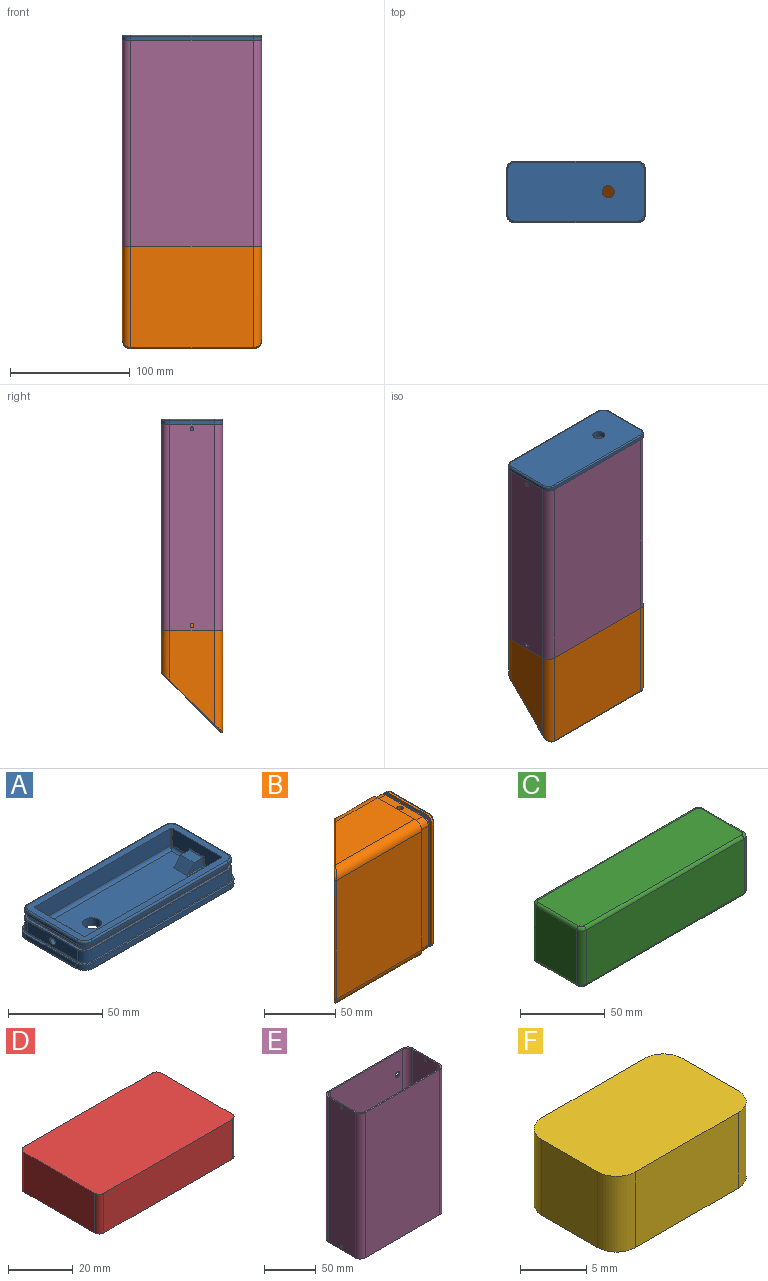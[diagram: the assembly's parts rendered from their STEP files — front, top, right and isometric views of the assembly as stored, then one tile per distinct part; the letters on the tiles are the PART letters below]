
ASSEMBLY  parts=6 mates=8
PART A: 138 faces, bbox 117.3x52.3x18.2 mm
  f0: cylinder r=0.5mm len=4mm, axis (0,0,-1), area 3.1mm2, adj f1,f3,f10,f116
  f1: torus R=1.5mm, axis (0,-1,0), area 2.2mm2, adj f0,f2,f3,f112
  f2: cylinder r=0.5mm len=10.03mm, axis (1,0,0), area 7.7mm2, adj f1,f3,f11,f12
  f3: plane 11.12x5.5mm, normal (0,1,0), area 48mm2, adj f0,f1,f2,f10,f11
  f4: cylinder r=0.5mm len=10.03mm, axis (-1,0,0), area 7.7mm2, adj f5,f7,f11,f12
  f5: torus R=1.5mm, axis (0,1,0), area 2.2mm2, adj f4,f6,f7,f13
  f6: cylinder r=0.5mm len=4mm, axis (0,0,1), area 3.1mm2, adj f5,f7,f10,f116
  f7: plane 11.12x5.5mm, normal (0,-1,0), area 48mm2, adj f4,f5,f6,f10,f11
  f8: cylinder r=2mm len=10mm, axis (1,0,0), area 125.7mm2, adj f9,f133
  f9: plane 4x4mm, normal (-1,0,0), area 12.6mm2, adj f8
  f10: plane 11x7mm, normal (0,0,1), area 70.1mm2, adj f0,f3,f6,f7,f11,f116
  f11: plane 11.18x6.18mm, normal (0.77,0,0.64), area 78.5mm2, adj f2,f3,f4,f7,f10,f12
  f12: plane 99x34mm, normal (0,0,1), area 3066.7mm2, adj f2,f4,f11,f13,f16,f20,f26,f28
  f13: cylinder r=2mm len=13mm, axis (0,-1,0), area 38.5mm2, adj f5,f12,f105,f116
  f14: cylinder r=0.5mm len=4.5mm, axis (0,0,-1), area 3.3mm2, adj f15,f19,f21,f27
  f15: cylinder r=0.5mm len=11mm, axis (0,-1,0), area 8.2mm2, adj f14,f18,f22,f27
  f16: cylinder r=0.5mm len=10.03mm, axis (1,0,0), area 7.7mm2, adj f12,f17,f23,f26
  f17: torus R=1.5mm, axis (0,-1,0), area 2.2mm2, adj f16,f18,f23,f110
  f18: cylinder r=0.5mm len=4.5mm, axis (0,0,1), area 3.3mm2, adj f15,f17,f23,f27
  f19: torus R=1.5mm, axis (0,1,0), area 2.2mm2, adj f14,f20,f21,f28
  f20: cylinder r=0.5mm len=10.03mm, axis (-1,0,0), area 7.7mm2, adj f12,f19,f21,f26
  f21: plane 11.12x5.5mm, normal (0,-1,0), area 48mm2, adj f14,f19,f20,f22,f26
  f22: plane 10x6.5mm, normal (0,0,1), area 65mm2, adj f15,f21,f23,f26
  f23: plane 11.12x5.5mm, normal (0,1,0), area 48mm2, adj f16,f17,f18,f22,f26
  f24: cylinder r=2mm len=10mm, axis (1,0,0), area 125.7mm2, adj f25,f37
  f25: plane 4x4mm, normal (1,0,0), area 12.6mm2, adj f24
  f26: plane 11.18x6.18mm, normal (-0.77,0,0.64), area 78.5mm2, adj f12,f16,f20,f21,f22,f23
  f27: plane 37x11mm, normal (-1,0,0), area 357.5mm2, adj f14,f15,f18,f28,f54,f110,f114,f115
  f28: cylinder r=2mm len=13mm, axis (0,1,0), area 38.5mm2, adj f12,f19,f27,f108
  f29: torus R=6mm, axis (0,0,1), area 7mm2, adj f30,f36,f40,f41
  f30: cylinder r=0.5mm len=37mm, axis (0,-1,0), area 29.1mm2, adj f29,f31,f41,f133
  f31: torus R=6mm, axis (0,0,1), area 7mm2, adj f30,f32,f41,f65
  f32: cylinder r=0.5mm len=102mm, axis (1,0,0), area 80.1mm2, adj f31,f33,f41,f64
  f33: torus R=6mm, axis (0,0,1), area 7mm2, adj f32,f34,f41,f63
  f34: cylinder r=0.5mm len=37mm, axis (0,1,0), area 29.1mm2, adj f33,f35,f37,f41
  f35: torus R=6mm, axis (0,0,1), area 7mm2, adj f34,f36,f38,f41
  f36: cylinder r=0.5mm len=102mm, axis (-1,0,0), area 80.1mm2, adj f29,f35,f39,f41
  f37: plane 37x7.3mm, normal (1,0,0), area 257.5mm2, adj f24,f34,f38,f60,f63
  f38: cylinder r=5.5mm len=7.3mm, axis (0,0,-1), area 63.1mm2, adj f35,f37,f39,f59
  f39: plane 102x7.3mm, normal (0,1,0), area 744.6mm2, adj f36,f38,f40,f58
  f40: cylinder r=5.5mm len=7.3mm, axis (0,0,-1), area 63.1mm2, adj f29,f39,f57,f133
  f41: plane 116x51mm, normal (0,0,1), area 318.8mm2, adj f29,f30,f31,f32,f33,f34,f35,f36
  f42: torus R=4.5mm, axis (0,0,1), area 12.7mm2, adj f43,f49,f53,f54
  f43: cylinder r=1mm len=37mm, axis (0,1,0), area 58.1mm2, adj f42,f44,f52,f54
  f44: torus R=4.5mm, axis (0,0,1), area 12.7mm2, adj f43,f45,f51,f54
  f45: cylinder r=1mm len=102mm, axis (-1,0,0), area 160.2mm2, adj f44,f46,f50,f54
  f46: torus R=4.5mm, axis (0,0,1), area 12.7mm2, adj f45,f47,f54,f103
  f47: cylinder r=1mm len=37mm, axis (0,-1,0), area 58.1mm2, adj f46,f48,f54,f75
  f48: torus R=4.5mm, axis (0,0,1), area 12.7mm2, adj f47,f49,f54,f76
  f49: cylinder r=1mm len=102mm, axis (1,0,0), area 160.2mm2, adj f42,f48,f54,f77
  f50: plane 102x1.8mm, normal (0,1,0), area 183.6mm2, adj f45,f51,f70,f103
  f51: cylinder r=5.5mm len=5.5mm, axis (0,0,-1), area 15.6mm2, adj f44,f50,f52,f69
  f52: plane 37x1.8mm, normal (1,0,0), area 66.6mm2, adj f43,f51,f53,f68
  f53: cylinder r=5.5mm len=5.5mm, axis (0,0,-1), area 15.6mm2, adj f42,f52,f67,f77
  f54: plane 111x46mm, normal (0,0,1), area 1174.8mm2, adj f27,f42,f43,f44,f45,f46,f47,f48
  f55: torus R=5.3mm, axis (0,0,-1), area 2.7mm2, adj f56,f62,f65,f66
  f56: cylinder r=0.2mm len=37mm, axis (0,1,0), area 11.6mm2, adj f55,f57,f66,f133
  f57: torus R=5.3mm, axis (0,0,-1), area 2.7mm2, adj f40,f56,f58,f66
  f58: cylinder r=0.2mm len=102mm, axis (1,0,0), area 32mm2, adj f39,f57,f59,f66
  f59: torus R=5.3mm, axis (0,0,-1), area 2.7mm2, adj f38,f58,f60,f66
  f60: cylinder r=0.2mm len=37mm, axis (0,-1,0), area 11.6mm2, adj f37,f59,f61,f66
  f61: torus R=5.3mm, axis (0,0,-1), area 2.7mm2, adj f60,f62,f63,f66
  f62: cylinder r=0.2mm len=102mm, axis (-1,0,0), area 32mm2, adj f55,f61,f64,f66
  f63: cylinder r=5.5mm len=7.3mm, axis (0,0,-1), area 63.1mm2, adj f33,f37,f61,f64
  f64: plane 102x7.3mm, normal (0,-1,0), area 744.6mm2, adj f32,f62,f63,f65
  f65: cylinder r=5.5mm len=7.3mm, axis (0,0,-1), area 63.1mm2, adj f31,f55,f64,f133
  f66: plane 112.6x47.6mm, normal (0,0,1), area 459.9mm2, adj f55,f56,f57,f58,f59,f60,f61,f62
  f67: torus R=5.3mm, axis (0,0,1), area 2.7mm2, adj f53,f68,f74,f78
  f68: cylinder r=0.2mm len=37mm, axis (0,1,0), area 11.6mm2, adj f52,f67,f69,f78
  f69: torus R=5.3mm, axis (0,0,1), area 2.7mm2, adj f51,f68,f70,f78
  f70: cylinder r=0.2mm len=102mm, axis (-1,0,0), area 32mm2, adj f50,f69,f71,f78
  f71: torus R=5.3mm, axis (0,0,1), area 2.7mm2, adj f70,f72,f78,f103
  f72: cylinder r=0.2mm len=37mm, axis (0,-1,0), area 11.6mm2, adj f71,f73,f75,f78
  f73: torus R=5.3mm, axis (0,0,1), area 2.7mm2, adj f72,f74,f76,f78
  f74: cylinder r=0.2mm len=102mm, axis (1,0,0), area 32mm2, adj f67,f73,f77,f78
  f75: plane 37x1.8mm, normal (-1,0,0), area 66.6mm2, adj f47,f72,f76,f103
  f76: cylinder r=5.5mm len=5.5mm, axis (0,0,-1), area 15.6mm2, adj f48,f73,f75,f77
  f77: plane 102x1.8mm, normal (0,-1,0), area 183.6mm2, adj f49,f53,f74,f76
  f78: plane 112.6x47.6mm, normal (0,0,-1), area 459.9mm2, adj f67,f68,f69,f70,f71,f72,f73,f74
  f79: torus R=3.8mm, axis (0,0,-1), area 2.7mm2, adj f66,f80,f86,f90
  f80: cylinder r=0.3mm len=37mm, axis (0,1,0), area 17.4mm2, adj f66,f79,f81,f89
  f81: torus R=3.8mm, axis (0,0,-1), area 2.7mm2, adj f66,f80,f82,f88
  f82: cylinder r=0.3mm len=102mm, axis (1,0,0), area 48.1mm2, adj f66,f81,f83,f87
  f83: torus R=3.8mm, axis (0,0,-1), area 2.7mm2, adj f66,f82,f84,f102
  f84: cylinder r=0.3mm len=37mm, axis (0,-1,0), area 17.4mm2, adj f66,f83,f85,f99
  f85: torus R=3.8mm, axis (0,0,-1), area 2.7mm2, adj f66,f84,f86,f100
  f86: cylinder r=0.3mm len=102mm, axis (-1,0,0), area 48.1mm2, adj f66,f79,f85,f101
  f87: plane 102x2.4mm, normal (0,1,0), area 244.8mm2, adj f82,f88,f94,f102
  f88: cylinder r=3.5mm len=3.5mm, axis (0,0,-1), area 13.2mm2, adj f81,f87,f89,f93
  f89: plane 37x2.4mm, normal (-1,0,0), area 88.8mm2, adj f80,f88,f90,f92
  f90: cylinder r=3.5mm len=3.5mm, axis (0,0,-1), area 13.2mm2, adj f79,f89,f91,f101
  f91: torus R=3.8mm, axis (0,0,-1), area 2.7mm2, adj f78,f90,f92,f98
  f92: cylinder r=0.3mm len=37mm, axis (0,1,0), area 17.4mm2, adj f78,f89,f91,f93
  f93: torus R=3.8mm, axis (0,0,-1), area 2.7mm2, adj f78,f88,f92,f94
  f94: cylinder r=0.3mm len=102mm, axis (1,0,0), area 48.1mm2, adj f78,f87,f93,f95
  f95: torus R=3.8mm, axis (0,0,-1), area 2.7mm2, adj f78,f94,f96,f102
  f96: cylinder r=0.3mm len=37mm, axis (0,-1,0), area 17.4mm2, adj f78,f95,f97,f99
  f97: torus R=3.8mm, axis (0,0,-1), area 2.7mm2, adj f78,f96,f98,f100
  f98: cylinder r=0.3mm len=102mm, axis (-1,0,0), area 48.1mm2, adj f78,f91,f97,f101
  f99: plane 37x2.4mm, normal (1,0,0), area 88.8mm2, adj f84,f96,f100,f102
  f100: cylinder r=3.5mm len=3.5mm, axis (0,0,-1), area 13.2mm2, adj f85,f97,f99,f101
  f101: plane 102x2.4mm, normal (0,-1,0), area 244.8mm2, adj f86,f90,f98,f100
  f102: cylinder r=3.5mm len=3.5mm, axis (0,0,-1), area 13.2mm2, adj f83,f87,f95,f99
  f103: cylinder r=5.5mm len=5.5mm, axis (0,0,-1), area 15.6mm2, adj f46,f50,f71,f75
  f104: cylinder r=5mm len=10mm, axis (0,0,-1), area 157.1mm2, adj f12,f132
  f105: bspline ~2x2mm, area 1.1mm2, adj f13,f109,f117
  f106: bspline ~2x2mm, area 1.1mm2, adj f111,f112,f119
  f107: bspline ~2x2mm, area 1.1mm2, adj f110,f111,f114
  f108: bspline ~2x2mm, area 1.1mm2, adj f28,f109,f115
  f109: cylinder r=2mm len=102mm, axis (1,0,0), area 315.7mm2, adj f12,f105,f108,f118
  f110: cylinder r=2mm len=13mm, axis (0,1,0), area 38.5mm2, adj f12,f17,f27,f107
  f111: cylinder r=2mm len=102mm, axis (-1,0,0), area 315.7mm2, adj f12,f106,f107,f113
  f112: cylinder r=2mm len=13mm, axis (0,-1,0), area 38.5mm2, adj f1,f12,f106,f116
  f113: plane 102x11mm, normal (0,-1,0), area 1122mm2, adj f54,f111,f114,f119
  f114: cylinder r=0.5mm len=11mm, axis (0,0,-1), area 8.6mm2, adj f27,f54,f107,f113
  f115: cylinder r=0.5mm len=11mm, axis (0,0,-1), area 8.6mm2, adj f27,f54,f108,f118
  f116: plane 37x11mm, normal (1,0,0), area 363mm2, adj f0,f6,f10,f13,f54,f112,f117,f119
  f117: cylinder r=0.5mm len=11mm, axis (0,0,-1), area 8.6mm2, adj f54,f105,f116,f118
  f118: plane 102x11mm, normal (0,1,0), area 1122mm2, adj f54,f109,f115,f117
  f119: cylinder r=0.5mm len=11mm, axis (0,0,-1), area 8.6mm2, adj f54,f106,f113,f116
  f120: torus R=6mm, axis (0,0,1), area 16.4mm2, adj f121,f127,f131,f132
  f121: cylinder r=1mm len=37mm, axis (0,-1,0), area 58.1mm2, adj f120,f122,f132,f136
  f122: torus R=6mm, axis (0,0,1), area 16.4mm2, adj f121,f123,f132,f135
  f123: cylinder r=1mm len=102mm, axis (1,0,0), area 160.2mm2, adj f122,f124,f132,f134
  f124: torus R=6mm, axis (0,0,1), area 16.4mm2, adj f123,f125,f132,f137
  f125: cylinder r=1mm len=37mm, axis (0,1,0), area 58.1mm2, adj f124,f126,f128,f132
  f126: torus R=6mm, axis (0,0,1), area 16.4mm2, adj f125,f127,f129,f132
  f127: cylinder r=1mm len=102mm, axis (-1,0,0), area 160.2mm2, adj f120,f126,f130,f132
  f128: plane 37x3mm, normal (1,0,0), area 111mm2, adj f41,f125,f129,f137
  f129: cylinder r=7mm len=7mm, axis (0,0,1), area 33mm2, adj f41,f126,f128,f130
  f130: plane 102x3mm, normal (0,1,0), area 306mm2, adj f41,f127,f129,f131
  f131: cylinder r=7mm len=7mm, axis (0,0,1), area 33mm2, adj f41,f120,f130,f136
  f132: plane 114x49mm, normal (0,0,-1), area 5476.6mm2, adj f104,f120,f121,f122,f123,f124,f125,f126
  f133: plane 37x7.3mm, normal (-1,0,0), area 257.5mm2, adj f8,f30,f40,f56,f65
  f134: plane 102x3mm, normal (0,-1,0), area 306mm2, adj f41,f123,f135,f137
  f135: cylinder r=7mm len=7mm, axis (0,0,1), area 33mm2, adj f41,f122,f134,f136
  f136: plane 37x3mm, normal (-1,0,0), area 111mm2, adj f41,f121,f131,f135
  f137: cylinder r=7mm len=7mm, axis (0,0,1), area 33mm2, adj f41,f124,f128,f134
PART B: 106 faces, bbox 100.1x51.4x116.4 mm
  f0: torus R=4.5mm, axis (1,0,0), area 12.7mm2, adj f1,f7,f11,f12
  f1: cylinder r=1mm len=37mm, axis (0,-1,0), area 58.1mm2, adj f0,f2,f10,f12
  f2: torus R=4.5mm, axis (1,0,0), area 12.7mm2, adj f1,f3,f9,f12
  f3: cylinder r=1mm len=102mm, axis (0,0,-1), area 160.2mm2, adj f2,f4,f8,f12
  f4: torus R=4.5mm, axis (1,0,0), area 12.7mm2, adj f3,f5,f12,f79
  f5: cylinder r=1mm len=37mm, axis (0,1,0), area 58.1mm2, adj f4,f6,f12,f51
  f6: torus R=4.5mm, axis (1,0,0), area 12.7mm2, adj f5,f7,f12,f52
  f7: cylinder r=1mm len=102mm, axis (0,0,1), area 160.2mm2, adj f0,f6,f12,f53
  f8: plane 102x1.8mm, normal (0,-1,0), area 183.6mm2, adj f3,f9,f46,f79
  f9: cylinder r=5.5mm len=5.5mm, axis (-1,0,0), area 15.6mm2, adj f2,f8,f10,f45
  f10: plane 37x1.8mm, normal (0,0,1), area 66.6mm2, adj f1,f9,f11,f44
  f11: cylinder r=5.5mm len=5.5mm, axis (-1,0,0), area 15.6mm2, adj f0,f10,f43,f53
  f12: plane 111x46mm, normal (1,0,0), area 1033.5mm2, adj f0,f1,f2,f3,f4,f5,f6,f7
  f13: cylinder r=1mm len=37.71mm, axis (-0.71,-0.71,0), area 82.2mm2, adj f14,f20,f24,f25
  f14: bspline ~7.71x7.07mm, area 25.5mm2, adj f13,f15,f25,f104
  f15: cylinder r=1mm len=102mm, axis (0,0,1), area 240.3mm2, adj f14,f16,f25,f105
  f16: bspline ~7.71x7mm, area 25.5mm2, adj f15,f17,f25,f94
  f17: cylinder r=1mm len=37.71mm, axis (0.71,0.71,0), area 82.2mm2, adj f16,f18,f25,f93
  f18: bspline ~7x7mm, area 13.6mm2, adj f17,f19,f21,f25
  f19: cylinder r=1mm len=102mm, axis (0,0,-1), area 80.1mm2, adj f18,f20,f22,f25
  f20: bspline ~7x7mm, area 13.6mm2, adj f13,f19,f23,f25
  f21: cylinder r=7mm len=41.59mm, axis (1,0,0), area 424.3mm2, adj f18,f22,f92,f93
  f22: plane 102x35.59mm, normal (0,1,0), area 3629.8mm2, adj f19,f21,f23,f92
  f23: cylinder r=7mm len=41.59mm, axis (-1,0,0), area 424.3mm2, adj f20,f22,f24,f92
  f24: plane 78.59x37mm, normal (0,0,1), area 2223.2mm2, adj f13,f23,f92,f104
  f25: plane 114.01x49.01mm, normal (-0.71,0.71,0), area 7856mm2, adj f13,f14,f15,f16,f17,f18,f19,f20
  f26: cylinder r=2.25mm len=4.5mm, axis (0,0,1), area 42.4mm2, adj f27,f91
  f27: plane 4.5x4.5mm, normal (0,0,-1), area 15.9mm2, adj f26
  f28: cylinder r=2.25mm len=4.5mm, axis (0,0,1), area 42.4mm2, adj f29,f38
  f29: plane 4.5x4.5mm, normal (0,0,1), area 15.9mm2, adj f28
  f30: torus R=5.3mm, axis (-1,0,0), area 2.7mm2, adj f31,f37,f41,f42
  f31: cylinder r=0.2mm len=37mm, axis (0,-1,0), area 11.6mm2, adj f30,f32,f42,f91
  f32: torus R=5.3mm, axis (-1,0,0), area 2.7mm2, adj f31,f33,f42,f80
  f33: cylinder r=0.2mm len=102mm, axis (0,0,1), area 32mm2, adj f32,f34,f42,f81
  f34: torus R=5.3mm, axis (-1,0,0), area 2.7mm2, adj f33,f35,f42,f82
  f35: cylinder r=0.2mm len=37mm, axis (0,1,0), area 11.6mm2, adj f34,f36,f38,f42
  f36: torus R=5.3mm, axis (-1,0,0), area 2.7mm2, adj f35,f37,f39,f42
  f37: cylinder r=0.2mm len=102mm, axis (0,0,-1), area 32mm2, adj f30,f36,f40,f42
  f38: plane 37x7.3mm, normal (0,0,1), area 254.2mm2, adj f28,f35,f39,f82,f85
  f39: cylinder r=5.5mm len=7.3mm, axis (-1,0,0), area 63.1mm2, adj f36,f38,f40,f84
  f40: plane 102x7.3mm, normal (0,1,0), area 744.6mm2, adj f37,f39,f41,f83
  f41: cylinder r=5.5mm len=7.3mm, axis (-1,0,0), area 63.1mm2, adj f30,f40,f90,f91
  f42: plane 112.6x47.6mm, normal (1,0,0), area 459.9mm2, adj f30,f31,f32,f33,f34,f35,f36,f37
  f43: torus R=5.3mm, axis (1,0,0), area 2.7mm2, adj f11,f44,f50,f54
  f44: cylinder r=0.2mm len=37mm, axis (0,-1,0), area 11.6mm2, adj f10,f43,f45,f54
  f45: torus R=5.3mm, axis (1,0,0), area 2.7mm2, adj f9,f44,f46,f54
  f46: cylinder r=0.2mm len=102mm, axis (0,0,-1), area 32mm2, adj f8,f45,f47,f54
  f47: torus R=5.3mm, axis (1,0,0), area 2.7mm2, adj f46,f48,f54,f79
  f48: cylinder r=0.2mm len=37mm, axis (0,1,0), area 11.6mm2, adj f47,f49,f51,f54
  f49: torus R=5.3mm, axis (1,0,0), area 2.7mm2, adj f48,f50,f52,f54
  f50: cylinder r=0.2mm len=102mm, axis (0,0,1), area 32mm2, adj f43,f49,f53,f54
  f51: plane 37x1.8mm, normal (0,0,-1), area 66.6mm2, adj f5,f48,f52,f79
  f52: cylinder r=5.5mm len=5.5mm, axis (-1,0,0), area 15.6mm2, adj f6,f49,f51,f53
  f53: plane 102x1.8mm, normal (0,1,0), area 183.6mm2, adj f7,f11,f50,f52
  f54: plane 112.6x47.6mm, normal (-1,0,0), area 459.9mm2, adj f43,f44,f45,f46,f47,f48,f49,f50
  f55: cylinder r=0.3mm len=37mm, axis (0,-1,0), area 17.4mm2, adj f54,f56,f62,f66
  f56: torus R=3.8mm, axis (1,0,0), area 2.7mm2, adj f54,f55,f57,f65
  f57: cylinder r=0.3mm len=102mm, axis (0,0,-1), area 48.1mm2, adj f54,f56,f58,f64
  f58: torus R=3.8mm, axis (1,0,0), area 2.7mm2, adj f54,f57,f59,f63
  f59: cylinder r=0.3mm len=37mm, axis (0,1,0), area 17.4mm2, adj f54,f58,f60,f75
  f60: torus R=3.8mm, axis (1,0,0), area 2.7mm2, adj f54,f59,f61,f76
  f61: cylinder r=0.3mm len=102mm, axis (0,0,1), area 48.1mm2, adj f54,f60,f62,f77
  f62: torus R=3.8mm, axis (1,0,0), area 2.7mm2, adj f54,f55,f61,f78
  f63: cylinder r=3.5mm len=3.5mm, axis (1,0,0), area 13.2mm2, adj f58,f64,f71,f75
  f64: plane 102x2.4mm, normal (0,-1,0), area 244.8mm2, adj f57,f63,f65,f70
  f65: cylinder r=3.5mm len=3.5mm, axis (1,0,0), area 13.2mm2, adj f56,f64,f66,f69
  f66: plane 37x2.4mm, normal (0,0,1), area 88.8mm2, adj f55,f65,f68,f78
  f67: torus R=3.8mm, axis (1,0,0), area 2.7mm2, adj f42,f68,f74,f78
  f68: cylinder r=0.3mm len=37mm, axis (0,-1,0), area 17.4mm2, adj f42,f66,f67,f69
  f69: torus R=3.8mm, axis (1,0,0), area 2.7mm2, adj f42,f65,f68,f70
  f70: cylinder r=0.3mm len=102mm, axis (0,0,-1), area 48.1mm2, adj f42,f64,f69,f71
  f71: torus R=3.8mm, axis (1,0,0), area 2.7mm2, adj f42,f63,f70,f72
  f72: cylinder r=0.3mm len=37mm, axis (0,1,0), area 17.4mm2, adj f42,f71,f73,f75
  f73: torus R=3.8mm, axis (1,0,0), area 2.7mm2, adj f42,f72,f74,f76
  f74: cylinder r=0.3mm len=102mm, axis (0,0,1), area 48.1mm2, adj f42,f67,f73,f77
  f75: plane 37x2.4mm, normal (0,0,-1), area 88.8mm2, adj f59,f63,f72,f76
  f76: cylinder r=3.5mm len=3.5mm, axis (1,0,0), area 13.2mm2, adj f60,f73,f75,f77
  f77: plane 102x2.4mm, normal (0,1,0), area 244.8mm2, adj f61,f74,f76,f78
  f78: cylinder r=3.5mm len=3.5mm, axis (1,0,0), area 13.2mm2, adj f62,f66,f67,f77
  f79: cylinder r=5.5mm len=5.5mm, axis (-1,0,0), area 15.6mm2, adj f4,f8,f47,f51
  f80: cylinder r=5.5mm len=7.3mm, axis (-1,0,0), area 63.1mm2, adj f32,f81,f88,f91
  f81: plane 102x7.3mm, normal (0,-1,0), area 744.6mm2, adj f33,f80,f82,f87
  f82: cylinder r=5.5mm len=7.3mm, axis (-1,0,0), area 63.1mm2, adj f34,f38,f81,f86
  f83: cylinder r=0.5mm len=102mm, axis (0,0,1), area 80.1mm2, adj f40,f84,f90,f92
  f84: torus R=6mm, axis (1,0,0), area 7mm2, adj f39,f83,f85,f92
  f85: cylinder r=0.5mm len=37mm, axis (0,-1,0), area 29.1mm2, adj f38,f84,f86,f92
  f86: torus R=6mm, axis (1,0,0), area 7mm2, adj f82,f85,f87,f92
  f87: cylinder r=0.5mm len=102mm, axis (0,0,-1), area 80.1mm2, adj f81,f86,f88,f92
  f88: torus R=6mm, axis (1,0,0), area 7mm2, adj f80,f87,f89,f92
  f89: cylinder r=0.5mm len=37mm, axis (0,1,0), area 29.1mm2, adj f88,f90,f91,f92
  f90: torus R=6mm, axis (1,0,0), area 7mm2, adj f41,f83,f89,f92
  f91: plane 37x7.3mm, normal (0,0,-1), area 254.2mm2, adj f26,f31,f41,f80,f89
  f92: plane 116x51mm, normal (1,0,0), area 318.8mm2, adj f21,f22,f23,f24,f83,f84,f85,f86
  f93: plane 78.59x37mm, normal (0,0,-1), area 2223.2mm2, adj f17,f21,f92,f94
  f94: cylinder r=7mm len=84.59mm, axis (-1,0,0), area 897.1mm2, adj f16,f92,f93,f105
  f95: cylinder r=1mm len=86.51mm, axis (-1,0,0), area 135.1mm2, adj f12,f96,f102,f103
  f96: plane 85.51x37mm, normal (0,0,1), area 2479.5mm2, adj f12,f95,f97,f103
  f97: cylinder r=1mm len=48.51mm, axis (1,0,0), area 75.4mm2, adj f12,f96,f101,f103
  f98: cylinder r=1mm len=48.51mm, axis (-1,0,0), area 75.4mm2, adj f12,f99,f101,f103
  f99: plane 85.51x37mm, normal (0,0,-1), area 2479.5mm2, adj f12,f98,f100,f103
  f100: cylinder r=1mm len=86.51mm, axis (1,0,0), area 135.1mm2, adj f12,f99,f102,f103
  f101: plane 102x47.51mm, normal (0,-1,0), area 4846.5mm2, adj f12,f97,f98,f103
  f102: plane 102x86.51mm, normal (0,1,0), area 8824.5mm2, adj f12,f95,f100,f103
  f103: plane 104.42x39.42mm, normal (0.71,-0.71,0), area 5734.8mm2, adj f95,f96,f97,f98,f99,f100,f101,f102
  f104: cylinder r=7mm len=84.59mm, axis (1,0,0), area 897.1mm2, adj f14,f24,f92,f105
  f105: plane 102x84.59mm, normal (0,-1,0), area 8627.8mm2, adj f15,f92,f94,f104
PART C: 26 faces, bbox 140.7x42.7x43 mm
  f0: torus R=2mm, axis (0,0,1), area 16.2mm2, adj f1,f7,f11,f12
  f1: cylinder r=2mm len=34mm, axis (0,1,0), area 106.8mm2, adj f0,f2,f12,f23
  f2: torus R=2mm, axis (0,0,1), area 16.2mm2, adj f1,f3,f12,f22
  f3: cylinder r=2mm len=132mm, axis (-1,0,0), area 414.7mm2, adj f2,f4,f12,f21
  f4: torus R=2mm, axis (0,0,1), area 16.2mm2, adj f3,f5,f12,f25
  f5: cylinder r=2mm len=34mm, axis (0,-1,0), area 106.8mm2, adj f4,f6,f8,f12
  f6: torus R=2mm, axis (0,0,1), area 16.2mm2, adj f5,f7,f9,f12
  f7: cylinder r=2mm len=132mm, axis (1,0,0), area 414.7mm2, adj f0,f6,f10,f12
  f8: plane 39x34mm, normal (-1,0,0), area 1326mm2, adj f5,f9,f16,f25
  f9: cylinder r=4mm len=39mm, axis (0,0,1), area 245mm2, adj f6,f8,f10,f15
  f10: plane 132x39mm, normal (0,-1,0), area 5148mm2, adj f7,f9,f11,f14
  f11: cylinder r=4mm len=39mm, axis (0,0,1), area 245mm2, adj f0,f10,f13,f23
  f12: plane 136x38mm, normal (0,0,-1), area 5164.6mm2, adj f0,f1,f2,f3,f4,f5,f6,f7
  f13: torus R=2mm, axis (0,0,-1), area 16.2mm2, adj f11,f14,f20,f24
  f14: cylinder r=2mm len=132mm, axis (1,0,0), area 414.7mm2, adj f10,f13,f15,f24
  f15: torus R=2mm, axis (0,0,-1), area 16.2mm2, adj f9,f14,f16,f24
  f16: cylinder r=2mm len=34mm, axis (0,-1,0), area 106.8mm2, adj f8,f15,f17,f24
  f17: torus R=2mm, axis (0,0,-1), area 16.2mm2, adj f16,f18,f24,f25
  f18: cylinder r=2mm len=132mm, axis (-1,0,0), area 414.7mm2, adj f17,f19,f21,f24
  f19: torus R=2mm, axis (0,0,-1), area 16.2mm2, adj f18,f20,f22,f24
  f20: cylinder r=2mm len=34mm, axis (0,1,0), area 106.8mm2, adj f13,f19,f23,f24
  f21: plane 132x39mm, normal (0,1,0), area 5148mm2, adj f3,f18,f22,f25
  f22: cylinder r=4mm len=39mm, axis (0,0,1), area 245mm2, adj f2,f19,f21,f23
  f23: plane 39x34mm, normal (1,0,0), area 1326mm2, adj f1,f11,f20,f22
  f24: plane 136x38mm, normal (0,0,1), area 5164.6mm2, adj f13,f14,f15,f16,f17,f18,f19,f20
  f25: cylinder r=4mm len=39mm, axis (0,0,1), area 245mm2, adj f4,f8,f17,f21
PART D: 10 faces, bbox 60x35x15 mm
  f0: cylinder r=2mm len=15mm, axis (0,0,1), area 47.1mm2, adj f1,f2,f6,f9
  f1: plane 31x15mm, normal (1,0,0), area 465mm2, adj f0,f2,f3,f9
  f2: plane 60x35mm, normal (0,0,1), area 2096.6mm2, adj f0,f1,f3,f4,f5,f6,f7,f8
  f3: cylinder r=2mm len=15mm, axis (0,0,1), area 47.1mm2, adj f1,f2,f4,f9
  f4: plane 56x15mm, normal (0,-1,0), area 840mm2, adj f2,f3,f7,f9
  f5: cylinder r=2mm len=15mm, axis (0,0,1), area 47.1mm2, adj f2,f6,f8,f9
  f6: plane 56x15mm, normal (0,1,0), area 840mm2, adj f0,f2,f5,f9
  f7: cylinder r=2mm len=15mm, axis (0,0,1), area 47.1mm2, adj f2,f4,f8,f9
  f8: plane 31x15mm, normal (-1,0,0), area 465mm2, adj f2,f5,f7,f9
  f9: plane 60x35mm, normal (0,0,-1), area 2096.6mm2, adj f0,f1,f3,f4,f5,f6,f7,f8
PART E: 26 faces, bbox 116x51x172 mm
  f0: cylinder r=1.62mm len=3.24mm, axis (-1,0,0), area 15.3mm2, adj f16,f21
  f1: cylinder r=1.62mm len=3.24mm, axis (-1,0,0), area 15.3mm2, adj f14,f24
  f2: cylinder r=1.62mm len=3.24mm, axis (-1,0,0), area 15.3mm2, adj f16,f21
  f3: cylinder r=1.62mm len=3.24mm, axis (-1,0,0), area 15.3mm2, adj f14,f24
  f4: cylinder r=3mm len=6mm, axis (0,1,0), area 28.3mm2, adj f11,f18
  f5: cylinder r=3mm len=6mm, axis (0,1,0), area 28.3mm2, adj f11,f18
  f6: cylinder r=3mm len=6mm, axis (0,1,0), area 28.3mm2, adj f11,f18
  f7: cylinder r=3mm len=6mm, axis (0,1,0), area 28.3mm2, adj f11,f18
  f8: plane 172x102mm, normal (0,-1,0), area 17544mm2, adj f12,f19,f22,f25
  f9: plane 172x99mm, normal (0,1,0), area 17028mm2, adj f12,f20,f23,f25
  f10: cylinder r=7mm len=172mm, axis (0,0,1), area 1891.2mm2, adj f11,f12,f24,f25
  f11: plane 172x102mm, normal (0,1,0), area 17430.9mm2, adj f4,f5,f6,f7,f10,f12,f15,f25
  f12: plane 116x51mm, normal (0,0,-1), area 492mm2, adj f8,f9,f10,f11,f13,f14,f15,f16
  f13: cylinder r=7mm len=172mm, axis (0,0,1), area 1891.2mm2, adj f12,f14,f18,f25
  f14: plane 172x34mm, normal (-1,0,0), area 5831.5mm2, adj f1,f3,f12,f13,f23,f25
  f15: cylinder r=7mm len=172mm, axis (0,0,1), area 1891.2mm2, adj f11,f12,f16,f25
  f16: plane 172x37mm, normal (-1,0,0), area 6347.5mm2, adj f0,f2,f12,f15,f19,f25
  f17: cylinder r=7mm len=172mm, axis (0,0,1), area 1891.2mm2, adj f12,f18,f21,f25
  f18: plane 172x99mm, normal (0,-1,0), area 16914.9mm2, adj f4,f5,f6,f7,f12,f13,f17,f25
  f19: cylinder r=7mm len=172mm, axis (0,0,1), area 1891.2mm2, adj f8,f12,f16,f25
  f20: cylinder r=7mm len=172mm, axis (0,0,1), area 1891.2mm2, adj f9,f12,f21,f25
  f21: plane 172x34mm, normal (1,0,0), area 5831.5mm2, adj f0,f2,f12,f17,f20,f25
  f22: cylinder r=7mm len=172mm, axis (0,0,1), area 1891.2mm2, adj f8,f12,f24,f25
  f23: cylinder r=7mm len=172mm, axis (0,0,1), area 1891.2mm2, adj f9,f12,f14,f25
  f24: plane 172x37mm, normal (1,0,0), area 6347.5mm2, adj f1,f3,f10,f12,f22,f25
  f25: plane 116x51mm, normal (0,0,1), area 492mm2, adj f8,f9,f10,f11,f13,f14,f15,f16
PART F: 10 faces, bbox 15x10x7 mm
  f0: cylinder r=2mm len=7mm, axis (0,0,1), area 22mm2, adj f1,f2,f8,f9
  f1: plane 7x6mm, normal (1,0,0), area 42mm2, adj f0,f2,f3,f9
  f2: plane 15x10mm, normal (0,0,-1), area 146.6mm2, adj f0,f1,f3,f4,f5,f6,f7,f8
  f3: cylinder r=2mm len=7mm, axis (0,0,1), area 22mm2, adj f1,f2,f4,f9
  f4: plane 11x7mm, normal (0,1,0), area 77mm2, adj f2,f3,f5,f9
  f5: cylinder r=2mm len=7mm, axis (0,0,1), area 22mm2, adj f2,f4,f6,f9
  f6: plane 7x6mm, normal (-1,0,0), area 42mm2, adj f2,f5,f7,f9
  f7: cylinder r=2mm len=7mm, axis (0,0,1), area 22mm2, adj f2,f6,f8,f9
  f8: plane 11x7mm, normal (0,-1,0), area 77mm2, adj f0,f2,f7,f9
  f9: plane 15x10mm, normal (0,0,1), area 146.6mm2, adj f0,f1,f3,f4,f5,f6,f7,f8
PLACE A rot(axis=(0,1,0),180deg) t=(-79.87,5.33,154.12)mm
PLACE B rot(axis=(0,-1,0),90deg) t=(-79.87,-20.17,-108.88)mm
PLACE C rot(axis=(0,-1,0),90deg) t=(-81.87,-18.67,-5.88)mm
PLACE D rot(axis=(-0.58,-0.58,-0.58),120deg) t=(-51.77,-18.67,64.12)mm
PLACE E t=(-79.87,5.33,-21.88)mm
PLACE F rot(axis=(1,0,0),90deg) t=(-47.87,-11.67,-5.48)mm
MATE planar C.f10 <-> E.f9  axis (0,-1,0) through (-103.37,-18.67,64.12)mm
MATE slider E.f10 <-> B.f6  axis (0,0,-1) through (-28.87,23.83,-21.88)mm
MATE parallel F.f1 <-> E.f24  axis (1,0,0) through (-40.37,-15.17,-5.48)mm
MATE planar D.f9 <-> E.f9  axis (0,-1,0) through (-51.77,-18.67,64.12)mm
MATE planar F.f9 <-> E.f9  axis (0,-1,0) through (-47.87,-18.67,-5.48)mm
MATE parallel D.f6 <-> E.f14  axis (1,0,0) through (-34.27,-11.17,64.12)mm
MATE parallel C.f12 <-> E.f24  axis (1,0,0) through (-81.87,2.33,64.12)mm
MATE slider A.f35 <-> E.f15  axis (0,0,-1) through (-130.87,23.83,150.12)mm
